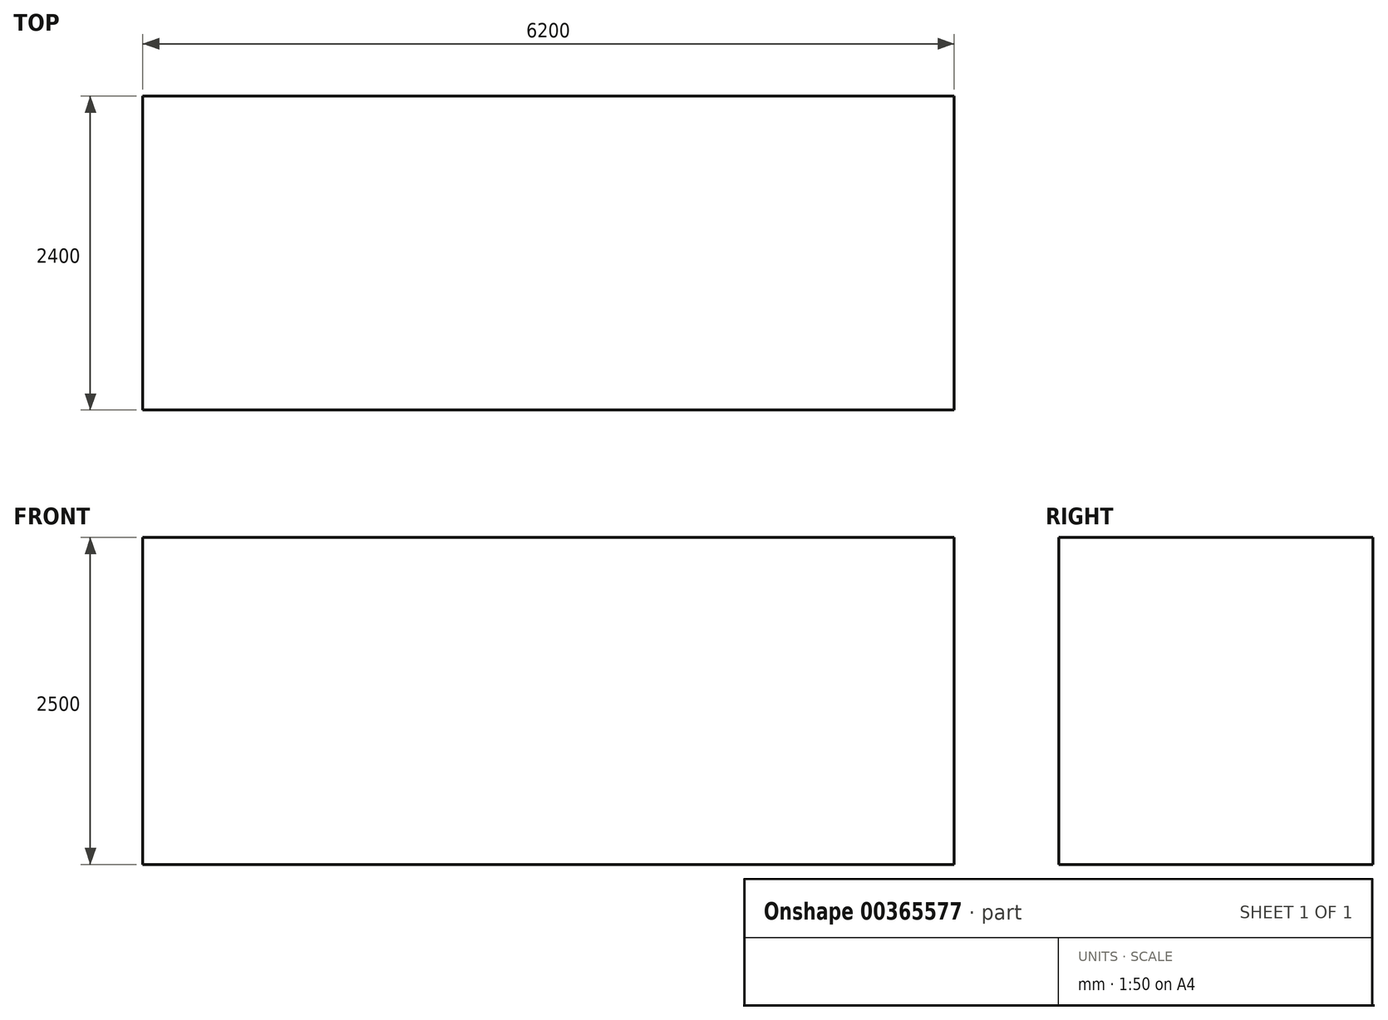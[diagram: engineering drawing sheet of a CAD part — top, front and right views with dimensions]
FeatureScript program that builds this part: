
annotation { "Feature Type Name" : "Feature", "Feature Type Description" : "" }
export const myFeature = defineFeature(function(context is Context, id is Id, definition is map)
    precondition{}
    {
        {
            var Q0;
            Q0=qCreatedBy(makeId("Top.planeOp"),FACE);
            var sketch = newSketch(context, id + "F0", { "sketchPlane" : qUnion([Q0])});
            skLineSegment(sketch, "E0.bottom", {"start": v(-3067.49, -2017.95) * mm, "end": v(3132.51, -2017.95) * mm});
            skLineSegment(sketch, "E0.top", {"start": v(-3067.49, 382.05) * mm, "end": v(3132.51, 382.05) * mm});
            skLineSegment(sketch, "E0.left", {"start": v(-3067.49, -2017.95) * mm, "end": v(-3067.49, 382.05) * mm});
            skLineSegment(sketch, "E0.right", {"start": v(3132.51, -2017.95) * mm, "end": v(3132.51, 382.05) * mm});
            skSolve(sketch);
        }
        {
            var Q0;
            Q0 = qSketchRegion(id + "F0", true);
            extrude(context, id + "F1", {"entities" : qUnion([Q0]), "depth" : 2500 * mm});
        }
    });
